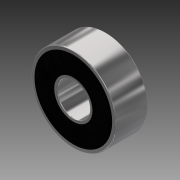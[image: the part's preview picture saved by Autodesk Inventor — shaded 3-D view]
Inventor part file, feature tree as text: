
AUTODESK INVENTOR PART (.ipt)
format: ipt  version: 2016 SP1 (Build 200210100, 210)  size: 180,224 bytes
history: native  units: in
note: dims shown in document units (in); Inventor stores cm internally (conversion verified against a paired STEP export)
features: sketch x2, extrude x1, fillet x1, revolve x1, plane x1, mirror x1
ambient origin geometry x8: Origin, YZ Plane, XZ Plane, XY Plane, X Axis, Y Axis, Z Axis, Center Point
bodies: Solid1 (feature_tree)
feature tree (7):
  extrude  "Extrusion1"  Depth=0.3937in
  fillet  "Fillet1"  Radius=0.3937in
  revolve  "Revolution1"  Angle=90.0deg
  plane  "Work Plane2"
  mirror  "Mirror2"
  sketch  "Sketch1"  dims[d0=0.3937in d1=1.0236in d2=0.3937in d3=0.0in]
  sketch  "Sketch2"  dims[d4=0.0118in d5=90.0deg d6=0.0197in d7=-0.1969in]
